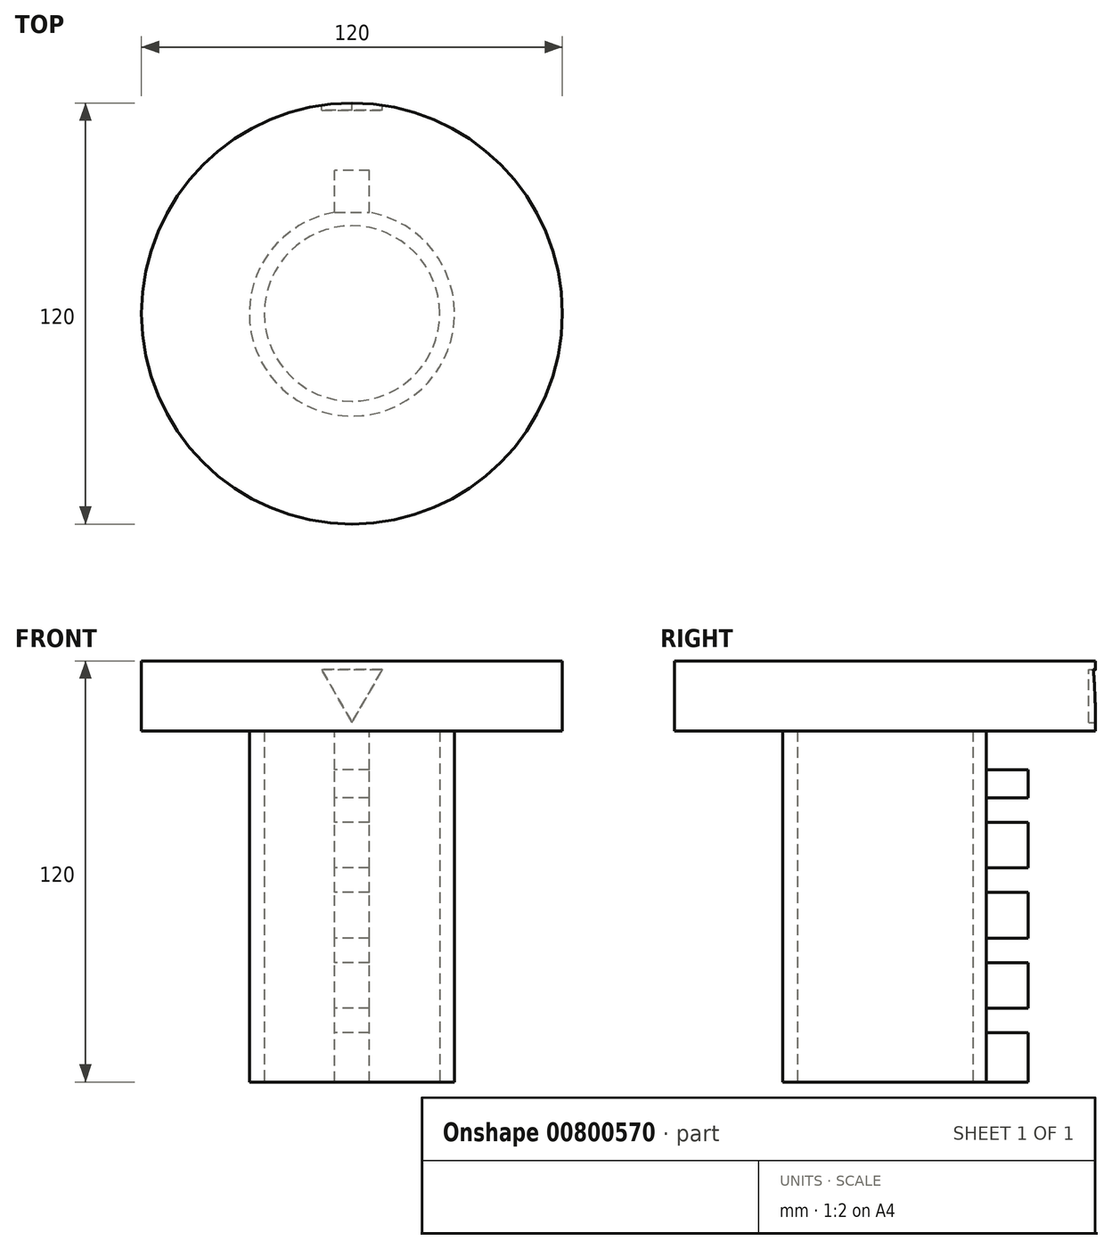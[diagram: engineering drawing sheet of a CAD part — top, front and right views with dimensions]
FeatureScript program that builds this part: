
annotation { "Feature Type Name" : "Feature", "Feature Type Description" : "" }
export const myFeature = defineFeature(function(context is Context, id is Id, definition is map)
    precondition{}
    {
        {
            var Q0;
            Q0=qCreatedBy(makeId("Top.planeOp"),FACE);
            var sketch = newSketch(context, id + "F0", { "sketchPlane" : qUnion([Q0])});
            skCircle(sketch, "E0", {"center": v(0, 0) * mm, "radius": 60 * mm});
            skSolve(sketch);
        }
        {
            var Q0;
            Q0=makeQuery(id+"F0.imprint","IMPRINT",FACE,{"disambiguationData":[TD([[makeQuery(id+"F0.imprint","IMPRINT",EDGE,{"derivedFrom":sQuery(id+"F0.wireOp",EDGE,"E0")}),1.0]])]});
            extrude(context, id + "F1", {"entities" : qUnion([Q0]), "depth" : 20 * mm, "offsetDistance" : 25.4 * mm});
        }
        {
            var Q0;
            Q0=makeQuery(id+"F1.opExtrude","CAP_FACE",FACE,{"disambiguationData":[OSD([sQuery(id+"F0.wireOp",EDGE,"E0")])],"isStart":true});
            var sketch = newSketch(context, id + "F2", { "sketchPlane" : qUnion([Q0])});
            skCircle(sketch, "E1", {"center": v(0, 0) * mm, "radius": 29.25 * mm});
            skSolve(sketch);
        }
        {
            var Q0;
            Q0=qSketchRegion(id+"F2",true);
            extrude(context, id + "F3", {"entities" : qUnion([Q0]), "operationType" : NewBodyOperationType.ADD, "depth" : 100 * mm, "offsetDistance" : 25.4 * mm});
        }
        {
            var Q0;
            Q0=makeQuery(id+"F3.opExtrude","CAP_FACE",FACE,{"disambiguationData":[OSD([sQuery(id+"F2.wireOp",EDGE,"E1")])],"isStart":false});
            var sketch = newSketch(context, id + "F4", { "sketchPlane" : qUnion([Q0])});
            skCircle(sketch, "E2", {"center": v(0, 0) * mm, "radius": 25 * mm});
            skLineSegment(sketch, "E3.bottom", {"start": v(10, -38.21) * mm, "end": v(-10, -38.21) * mm});
            skLineSegment(sketch, "E3.top", {"start": v(10, -25.71) * mm, "end": v(-10, -25.71) * mm});
            skLineSegment(sketch, "E3.left", {"start": v(10, -38.21) * mm, "end": v(10, -25.71) * mm});
            skLineSegment(sketch, "E3.right", {"start": v(-10, -38.21) * mm, "end": v(-10, -25.71) * mm});
            skLineSegment(sketch, "E4", {"start": v(0, 0) * mm, "end": v(0, -62.66) * mm, "construction": true});
            skLineSegment(sketch, "E5", {"start": v(0, -25.71) * mm, "end": v(0, -38.21) * mm});
            skSolve(sketch);
        }
        {
            var Q0;
            Q0=makeQuery(id+"F4.imprint","IMPRINT",FACE,{"disambiguationData":[TD([[makeQuery(id+"F4.imprint","IMPRINT",EDGE,{"derivedFrom":sQuery(id+"F4.wireOp",EDGE,"E2")}),1.0]])]});
            extrude(context, id + "F5", {"entities" : qUnion([Q0]), "operationType" : NewBodyOperationType.REMOVE, "oppositeDirection" : true, "depth" : 100 * mm, "offsetDistance" : 25.4 * mm});
        }
        {
            var Q0;
            Q0=makeQuery(id+"F5.boolean.opBoolean","COPY",FACE,{"derivedFrom":makeQuery(id+"F5.opExtrude","CAP_FACE",FACE,{"disambiguationData":[OSD([sQuery(id+"F4.wireOp",EDGE,"E2")])],"isStart":false})});
            var sketch = newSketch(context, id + "F6", { "sketchPlane" : qUnion([Q0])});
            skLineSegment(sketch, "E6.bottom", {"start": v(-5, -28.83) * mm, "end": v(5, -28.83) * mm});
            skLineSegment(sketch, "E6.top", {"start": v(-5, -40.83) * mm, "end": v(5, -40.83) * mm});
            skLineSegment(sketch, "E6.left", {"start": v(-5, -28.83) * mm, "end": v(-5, -40.83) * mm});
            skLineSegment(sketch, "E6.right", {"start": v(5, -28.83) * mm, "end": v(5, -40.83) * mm});
            skLineSegment(sketch, "E7", {"start": v(0, 0) * mm, "end": v(0, -50.42) * mm});
            skLineSegment(sketch, "E8", {"start": v(0, -40.83) * mm, "end": v(0, -28.83) * mm});
            skSolve(sketch);
        }
        {
            var Q0;
            Q0 = qSketchRegion(id + "F6", true);
            extrude(context, id + "F7", {"entities" : qUnion([Q0]), "operationType" : NewBodyOperationType.ADD, "depth" : 100 * mm, "offsetDistance" : 25 * mm});
        }
        {
            var Q0;
            Q0=makeQuery(id+"F7.opExtrude","SWEPT_FACE",FACE,{"disambiguationData":[OSD([sQuery(id+"F6.wireOp",EDGE,"E6.top")])]});
            var sketch = newSketch(context, id + "F8", { "sketchPlane" : qUnion([Q0])});
            skLineSegment(sketch, "E9.bottom", {"start": v(-5, -19) * mm, "end": v(5, -19) * mm});
            skLineSegment(sketch, "E9.top", {"start": v(-5, -11) * mm, "end": v(5, -11) * mm});
            skLineSegment(sketch, "E9.left", {"start": v(-5, -19) * mm, "end": v(-5, -11) * mm});
            skLineSegment(sketch, "E9.right", {"start": v(5, -19) * mm, "end": v(5, -11) * mm});
            skLineSegment(sketch, "E10.bottom", {"start": v(-5, -39) * mm, "end": v(5, -39) * mm});
            skLineSegment(sketch, "E10.top", {"start": v(-5, -26) * mm, "end": v(5, -26) * mm});
            skLineSegment(sketch, "E10.left", {"start": v(-5, -39) * mm, "end": v(-5, -26) * mm});
            skLineSegment(sketch, "E10.right", {"start": v(5, -39) * mm, "end": v(5, -26) * mm});
            skLineSegment(sketch, "E11.bottom", {"start": v(-5, -59) * mm, "end": v(5, -59) * mm});
            skLineSegment(sketch, "E11.top", {"start": v(-5, -46) * mm, "end": v(5, -46) * mm});
            skLineSegment(sketch, "E11.left", {"start": v(-5, -59) * mm, "end": v(-5, -46) * mm});
            skLineSegment(sketch, "E11.right", {"start": v(5, -59) * mm, "end": v(5, -46) * mm});
            skLineSegment(sketch, "E12.bottom", {"start": v(-5, -100) * mm, "end": v(5, -100) * mm});
            skLineSegment(sketch, "E12.top", {"start": v(-5, -86) * mm, "end": v(5, -86) * mm});
            skLineSegment(sketch, "E12.left", {"start": v(-5, -100) * mm, "end": v(-5, -86) * mm});
            skLineSegment(sketch, "E12.right", {"start": v(5, -100) * mm, "end": v(5, -86) * mm});
            skLineSegment(sketch, "E13.bottom", {"start": v(-5, -79) * mm, "end": v(5, -79) * mm});
            skLineSegment(sketch, "E13.top", {"start": v(-5, -66) * mm, "end": v(5, -66) * mm});
            skLineSegment(sketch, "E13.left", {"start": v(-5, -79) * mm, "end": v(-5, -66) * mm});
            skLineSegment(sketch, "E13.right", {"start": v(5, -79) * mm, "end": v(5, -66) * mm});
            skSolve(sketch);
        }
        {
            var Q0;
            {var subQ0=sQuery(id+"F8.wireOp",EDGE,"E12.top");Q0=makeQuery(id+"F8.imprint","IMPRINT",FACE,{"disambiguationData":[TD([[makeQuery(id+"F8.imprint","IMPRINT",EDGE,{"derivedFrom":subQ0}),1.0]])]});}
            var Q1;
            {var subQ0=sQuery(id+"F8.wireOp",EDGE,"E11.bottom");Q1=makeQuery(id+"F8.imprint","IMPRINT",FACE,{"disambiguationData":[TD([[makeQuery(id+"F8.imprint","IMPRINT",EDGE,{"derivedFrom":subQ0}),-1.0]])]});}
            var Q2;
            {var subQ0=sQuery(id+"F8.wireOp",EDGE,"E10.bottom");Q2=makeQuery(id+"F8.imprint","IMPRINT",FACE,{"disambiguationData":[TD([[makeQuery(id+"F8.imprint","IMPRINT",EDGE,{"derivedFrom":subQ0}),-1.0]])]});}
            var Q3;
            {var subQ0=sQuery(id+"F8.wireOp",EDGE,"E9.bottom");Q3=makeQuery(id+"F8.imprint","IMPRINT",FACE,{"disambiguationData":[TD([[makeQuery(id+"F8.imprint","IMPRINT",EDGE,{"derivedFrom":subQ0}),-1.0]])]});}
            var Q4;
            {var subQ0=sQuery(id+"F8.wireOp",EDGE,"E9.top");Q4=makeQuery(id+"F8.imprint","IMPRINT",FACE,{"disambiguationData":[TD([[makeQuery(id+"F8.imprint","IMPRINT",EDGE,{"derivedFrom":subQ0}),1.0]])]});}
            extrude(context, id + "F9", {"entities" : qUnion([Q0, Q1, Q2, Q3, Q4]), "operationType" : NewBodyOperationType.REMOVE, "oppositeDirection" : true, "depth" : 12 * mm, "offsetDistance" : 25 * mm});
        }
        {
            var Q0;
            Q0=qCreatedBy(makeId("Front.planeOp"),FACE);
            cPlane(context, id + "F10", {"entities" : qUnion([Q0]), "cplaneType" : CPlaneType.OFFSET, "offset" : 60 * mm, "oppositeDirection" : true, "width" : 150 * mm, "height" : 150 * mm});
        }
        {
            var Q0;
            Q0=qCreatedBy(id+"F10.planeOp",FACE);
            var sketch = newSketch(context, id + "F11", { "sketchPlane" : qUnion([Q0])});
            skCircle(sketch, "E14.cCircle", {"center": v(0, 12.5) * mm, "radius": 5 * mm, "construction": true});
            skLineSegment(sketch, "E14.0", {"start": v(0, 2.5) * mm, "end": v(-8.66, 17.5) * mm});
            skLineSegment(sketch, "E14.1", {"start": v(-8.66, 17.5) * mm, "end": v(8.66, 17.5) * mm});
            skLineSegment(sketch, "E14.2", {"start": v(8.66, 17.5) * mm, "end": v(0, 2.5) * mm});
            skPoint(sketch, "E14.0.midPoint", {"position": v(-4.33, 10) * mm});
            skSolve(sketch);
        }
        {
            var Q0;
            Q0 = qSketchRegion(id + "F11", true);
            extrude(context, id + "F12", {"entities" : qUnion([Q0]), "operationType" : NewBodyOperationType.REMOVE, "oppositeDirection" : true, "depth" : -2 * mm, "offsetDistance" : 25 * mm});
        }
    });
